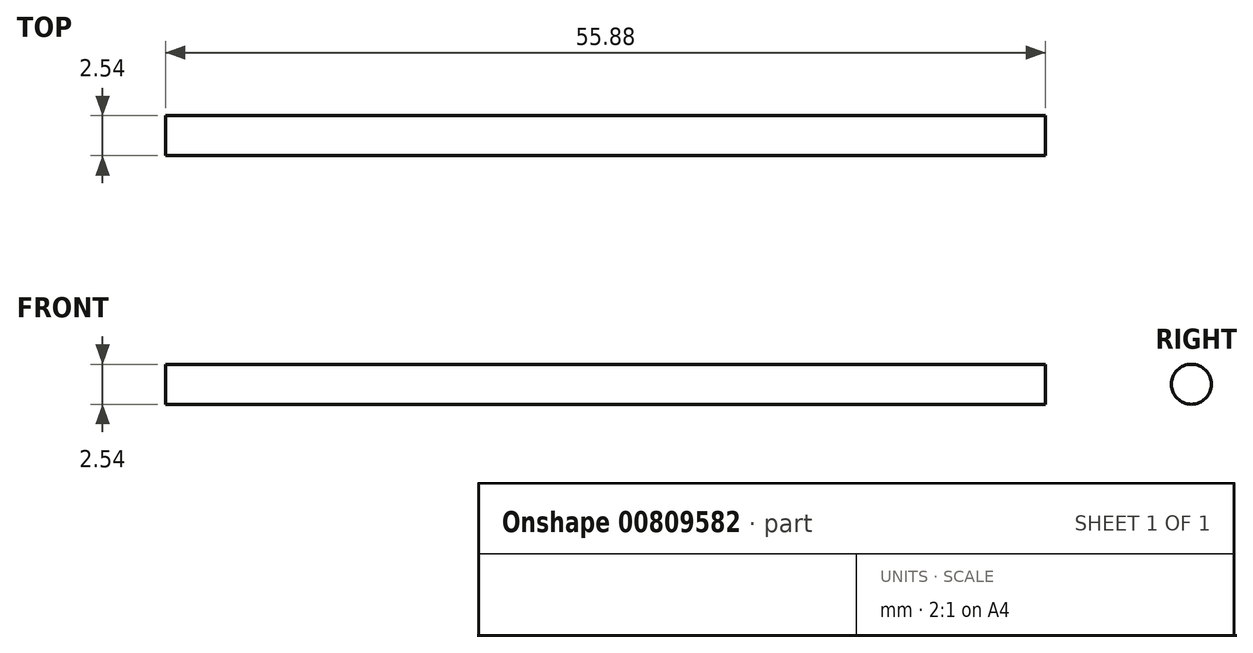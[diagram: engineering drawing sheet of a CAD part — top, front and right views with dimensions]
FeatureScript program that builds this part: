
annotation { "Feature Type Name" : "Feature", "Feature Type Description" : "" }
export const myFeature = defineFeature(function(context is Context, id is Id, definition is map)
    precondition{}
    {
        {
            var Q0;
            Q0=qCreatedBy(makeId("Right.planeOp"),FACE);
            var sketch = newSketch(context, id + "F0", { "sketchPlane" : qUnion([Q0])});
            skCircle(sketch, "E0", {"center": v(0, 0) * mm, "radius": 1.27 * mm});
            skSolve(sketch);
        }
        {
            var Q0;
            Q0 = qSketchRegion(id + "F0", true);
            extrude(context, id + "F1", {"entities" : qUnion([Q0]), "endBound" : BoundingType.SYMMETRIC, "depth" : 55.88 * mm, "offsetDistance" : 25.4 * mm});
        }
    });
